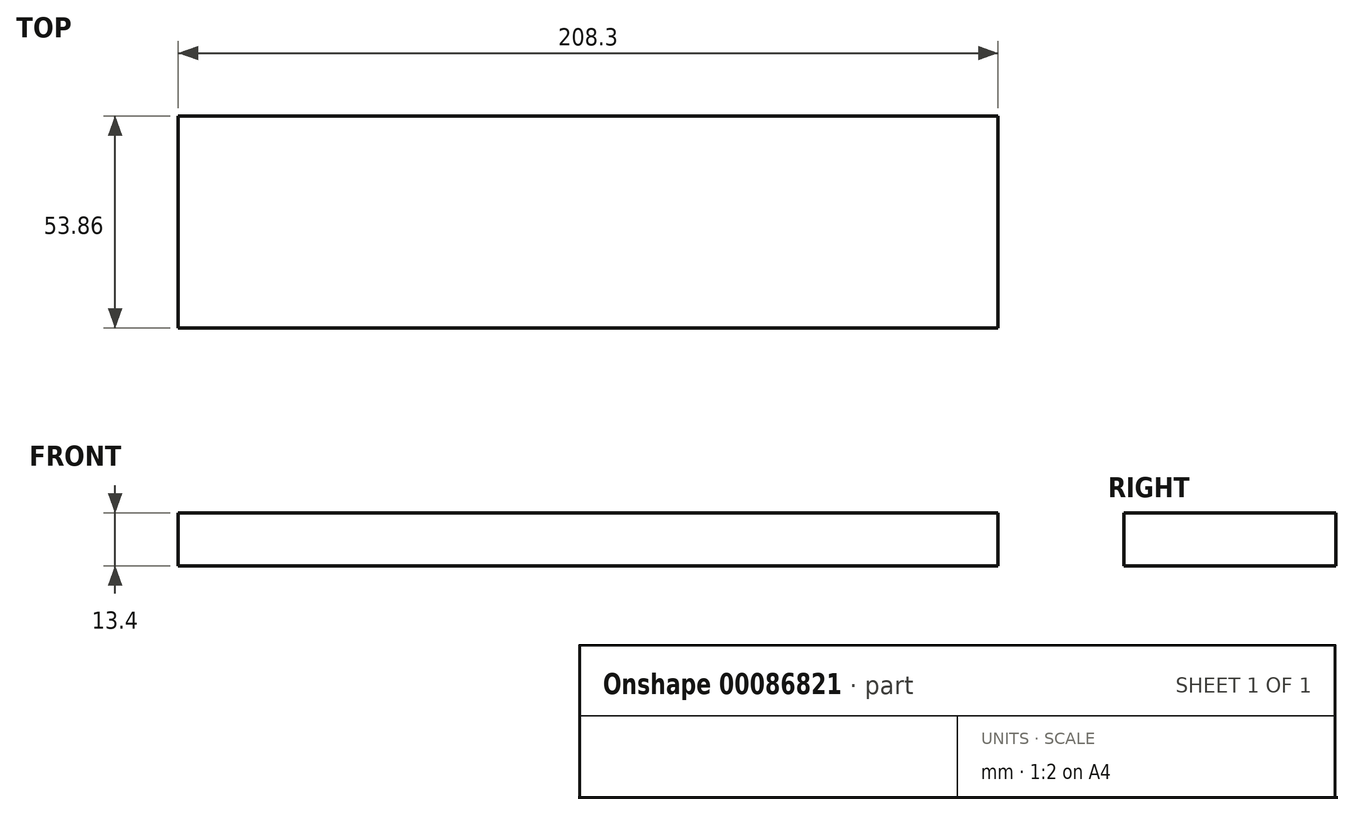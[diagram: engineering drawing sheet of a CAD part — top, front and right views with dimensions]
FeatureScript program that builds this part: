
annotation { "Feature Type Name" : "Feature", "Feature Type Description" : "" }
export const myFeature = defineFeature(function(context is Context, id is Id, definition is map)
    precondition{}
    {
        {
            var Q0;
            Q0=qCreatedBy(makeId("Front.planeOp"),FACE);
            var sketch = newSketch(context, id + "F0", { "sketchPlane" : qUnion([Q0])});
            skLineSegment(sketch, "E0.bottom", {"start": v(104.15, -6.7) * mm, "end": v(-104.15, -6.7) * mm});
            skLineSegment(sketch, "E0.top", {"start": v(104.15, 6.7) * mm, "end": v(-104.15, 6.7) * mm});
            skLineSegment(sketch, "E0.left", {"start": v(104.15, -6.7) * mm, "end": v(104.15, 6.7) * mm});
            skLineSegment(sketch, "E0.right", {"start": v(-104.15, -6.7) * mm, "end": v(-104.15, 6.7) * mm});
            skPoint(sketch, "E0.middle", {"position": v(0, 0) * mm});
            skSolve(sketch);
        }
        {
            var Q0;
            Q0 = qSketchRegion(id + "F0", true);
            extrude(context, id + "F1", {"entities" : qUnion([Q0]), "depth" : 53.86 * mm});
        }
    });
